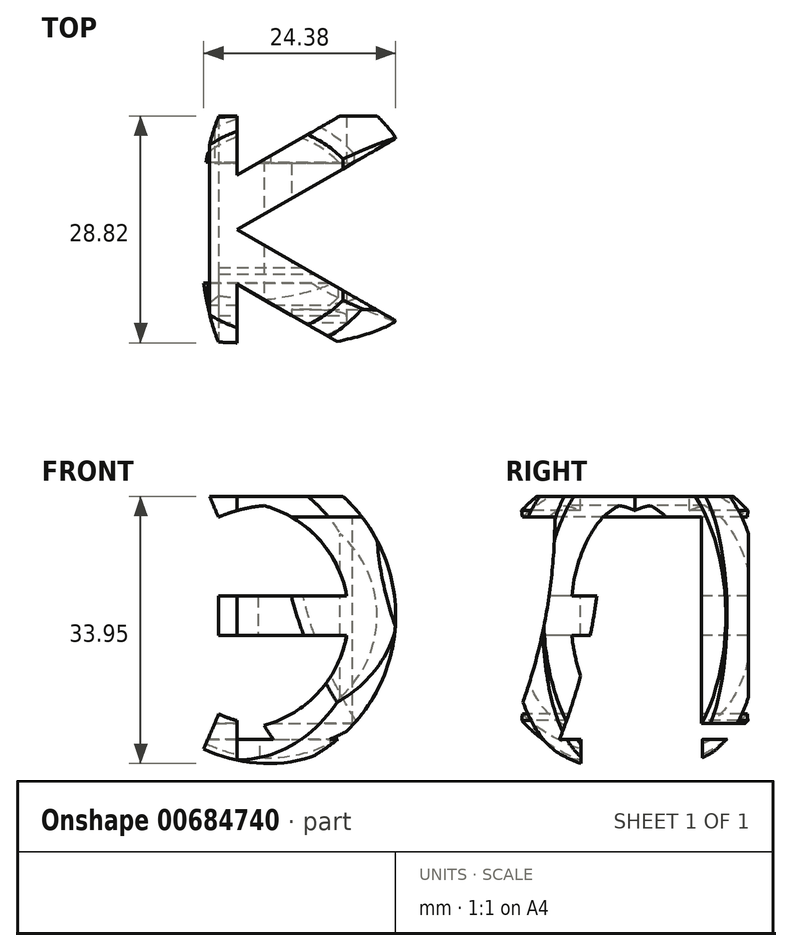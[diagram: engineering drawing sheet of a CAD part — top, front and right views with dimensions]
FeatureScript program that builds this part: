
annotation { "Feature Type Name" : "Feature", "Feature Type Description" : "" }
export const myFeature = defineFeature(function(context is Context, id is Id, definition is map)
    precondition{}
    {
        {
            var Q0;
            Q0=qCreatedBy(makeId("Front.planeOp"),FACE);
            var sketch = newSketch(context, id + "F0", { "sketchPlane" : qUnion([Q0])});
            skArc(sketch, "E0", {"start": v(20, 22.63) * mm, "mid": v(0, 42.63) * mm, "end": v(-20, 22.63) * mm});
            skLineSegment(sketch, "E1", {"start": v(20, 22.63) * mm, "end": v(0, 22.63) * mm});
            skLineSegment(sketch, "E2.MirrorCS", {"start": v(-20, 22.63) * mm, "end": v(0, 22.63) * mm});
            skSolve(sketch);
        }
        {
            var Q0;
            Q0=makeQuery(id+"F0.imprint","IMPRINT",FACE,{"disambiguationData":[TD([[makeQuery(id+"F0.imprint","IMPRINT",EDGE,{"derivedFrom":sQuery(id+"F0.wireOp",EDGE,"E0")}),1.0]])]});
            var Q1;
            Q1=sQuery(id+"F0.wireOp",EDGE,"E2.MirrorCS");
            revolve(context, id + "F1", {"entities" : qUnion([Q0]), "axis" : qUnion([Q1]), "revolveType" : RevolveType.FULL});
        }
        {
            var Q0;
            Q0=qCreatedBy(makeId("Top.planeOp"),FACE);
            cPlane(context, id + "F2", {"entities" : qUnion([Q0]), "cplaneType" : CPlaneType.OFFSET, "offset" : 43.3 * mm, "width" : 150 * mm, "height" : 150 * mm});
        }
        {
            var Q0;
            Q0=qCreatedBy(makeId("Right.planeOp"),FACE);
            cPlane(context, id + "F3", {"entities" : qUnion([Q0]), "cplaneType" : CPlaneType.OFFSET, "offset" : 22 * mm, "width" : 150 * mm, "height" : 150 * mm});
        }
        {
            var Q0;
            Q0=qCreatedBy(makeId("Front.planeOp"),FACE);
            cPlane(context, id + "F4", {"entities" : qUnion([Q0]), "cplaneType" : CPlaneType.OFFSET, "offset" : 22 * mm, "width" : 150 * mm, "height" : 150 * mm});
        }
        {
            var Q0;
            Q0=qCreatedBy(id+"F2.planeOp",FACE);
            var sketch = newSketch(context, id + "F5", { "sketchPlane" : qUnion([Q0])});
            skLineSegment(sketch, "E3", {"start": v(-11.94, 16.04) * mm, "end": v(-11.94, -16.04) * mm});
            skLineSegment(sketch, "E4", {"start": v(-11.94, -16.04) * mm, "end": v(-3.94, -16.04) * mm});
            skLineSegment(sketch, "E5", {"start": v(-3.94, -16.04) * mm, "end": v(-3.94, -6.92) * mm});
            skLineSegment(sketch, "E6", {"start": v(-3.94, -6.92) * mm, "end": v(11.94, -16.04) * mm});
            skLineSegment(sketch, "E7", {"start": v(16.28, -11.61) * mm, "end": v(-3.94, 0) * mm});
            skLineSegment(sketch, "E8", {"start": v(-3.94, 0) * mm, "end": v(16.28, 11.61) * mm});
            skLineSegment(sketch, "E9", {"start": v(11.94, 16.04) * mm, "end": v(-3.94, 6.92) * mm});
            skLineSegment(sketch, "E10", {"start": v(-3.94, 6.92) * mm, "end": v(-3.94, 16.04) * mm});
            skLineSegment(sketch, "E11", {"start": v(-3.94, 16.04) * mm, "end": v(-11.94, 16.04) * mm});
            skPoint(sketch, "E12.0", {"position": v(0, 0) * mm});
            skCircle(sketch, "E13", {"center": v(0, 0) * mm, "radius": 20 * mm});
            skPoint(sketch, "E14", {"position": v(-11.94, 0) * mm});
            skLineSegment(sketch, "E15", {"start": v(-11.94, 16.04) * mm, "end": v(17.44, 16.04) * mm, "construction": true});
            skLineSegment(sketch, "E16", {"start": v(-11.94, -16.04) * mm, "end": v(18.16, -16.04) * mm, "construction": true});
            skLineSegment(sketch, "E17", {"start": v(15.03, 16.04) * mm, "end": v(11.94, 16.04) * mm});
            skLineSegment(sketch, "E18", {"start": v(15.03, -16.04) * mm, "end": v(11.94, -16.04) * mm});
            skSolve(sketch);
        }
        {
            var Q0;
            {var subQ0=sQuery(id+"F5.wireOp",EDGE,"E3");Q0=makeQuery(id+"F5.imprint","IMPRINT",FACE,{"disambiguationData":[TD([[makeQuery(id+"F5.imprint","IMPRINT",EDGE,{"derivedFrom":subQ0}),-1.0]])]});}
            var Q1;
            {var subQ0=sQuery(id+"F5.wireOp",EDGE,"E4");Q1=makeQuery(id+"F5.imprint","IMPRINT",FACE,{"disambiguationData":[TD([[makeQuery(id+"F5.imprint","IMPRINT",EDGE,{"derivedFrom":subQ0}),-1.0]])]});}
            var Q2;
            {var subQ0=sQuery(id+"F5.wireOp",EDGE,"E7");Q2=makeQuery(id+"F5.imprint","IMPRINT",FACE,{"disambiguationData":[TD([[makeQuery(id+"F5.imprint","IMPRINT",EDGE,{"derivedFrom":subQ0}),-1.0]])]});}
            var Q3;
            {var subQ0=sQuery(id+"F5.wireOp",EDGE,"E9");Q3=makeQuery(id+"F5.imprint","IMPRINT",FACE,{"disambiguationData":[TD([[makeQuery(id+"F5.imprint","IMPRINT",EDGE,{"derivedFrom":subQ0}),-1.0]])]});}
            extrude(context, id + "F6", {"entities" : qUnion([Q0, Q1, Q2, Q3]), "operationType" : NewBodyOperationType.REMOVE, "oppositeDirection" : true, "depth" : 48.9 * mm, "offsetDistance" : 25 * mm});
        }
        {
            var Q0;
            Q0=qCreatedBy(id+"F4.planeOp",FACE);
            var sketch = newSketch(context, id + "F7", { "sketchPlane" : qUnion([Q0])});
            skPoint(sketch, "E19.0", {"position": v(0, 22.63) * mm});
            skCircle(sketch, "E20", {"center": v(0, 22.63) * mm, "radius": 20 * mm});
            skArc(sketch, "E21", {"start": v(0, 2.63) * mm, "mid": v(16.21, 22.63) * mm, "end": v(0, 42.63) * mm});
            skArc(sketch, "E22", {"start": v(0, 42.63) * mm, "mid": v(-4.41, 42.04) * mm, "end": v(-8.65, 40.67) * mm});
            skArc(sketch, "E23", {"start": v(-8.65, 4.6) * mm, "mid": v(-4.41, 3.22) * mm, "end": v(0, 2.63) * mm});
            skLineSegment(sketch, "E24", {"start": v(-8.65, 40.67) * mm, "end": v(-8.65, 4.6) * mm, "construction": true});
            skLineSegment(sketch, "E25", {"start": v(-6.65, 41.42) * mm, "end": v(-6.65, 3.77) * mm, "construction": true});
            skArc(sketch, "E26.0", {"start": v(-1.24, 8.5) * mm, "mid": v(10.21, 22.63) * mm, "end": v(-1.24, 36.76) * mm});
            skArc(sketch, "E27.0", {"start": v(0.28, 36.64) * mm, "mid": v(-3.08, 36.18) * mm, "end": v(-6.3, 35.14) * mm});
            skArc(sketch, "E28.0", {"start": v(-6.26, 10.1) * mm, "mid": v(-3.08, 9.07) * mm, "end": v(0.23, 8.63) * mm});
            skLineSegment(sketch, "E29", {"start": v(-8.65, 40.67) * mm, "end": v(-6.3, 35.14) * mm});
            skLineSegment(sketch, "E30", {"start": v(-8.65, 4.6) * mm, "end": v(-6.26, 10.1) * mm});
            skLineSegment(sketch, "E31", {"start": v(-6.26, 22.63) * mm, "end": v(10.21, 22.63) * mm, "construction": true});
            skLineSegment(sketch, "E32", {"start": v(-6.26, 25.13) * mm, "end": v(10, 25.13) * mm});
            skLineSegment(sketch, "E33", {"start": v(-6.26, 20.13) * mm, "end": v(10, 20.13) * mm});
            skLineSegment(sketch, "E34", {"start": v(-6.26, 25.13) * mm, "end": v(-6.26, 20.13) * mm});
            skSolve(sketch);
        }
        {
            var Q0;
            {var subQ0=sQuery(id+"F7.wireOp",EDGE,"E22");Q0=makeQuery(id+"F7.imprint","IMPRINT",FACE,{"disambiguationData":[TD([[makeQuery(id+"F7.imprint","IMPRINT",EDGE,{"derivedFrom":subQ0}),-1.0]])]});}
            var Q1;
            {var subQ0=sQuery(id+"F7.wireOp",EDGE,"E23");Q1=makeQuery(id+"F7.imprint","IMPRINT",FACE,{"disambiguationData":[TD([[makeQuery(id+"F7.imprint","IMPRINT",EDGE,{"derivedFrom":subQ0}),-1.0]])]});}
            var Q2;
            {var subQ0=sQuery(id+"F7.wireOp",EDGE,"E21");Q2=makeQuery(id+"F7.imprint","IMPRINT",FACE,{"disambiguationData":[TD([[makeQuery(id+"F7.imprint","IMPRINT",EDGE,{"derivedFrom":subQ0}),-1.0]])]});}
            var Q3;
            {var subQ0=sQuery(id+"F7.wireOp",EDGE,"E29");Q3=makeQuery(id+"F7.imprint","IMPRINT",FACE,{"disambiguationData":[TD([[makeQuery(id+"F7.imprint","IMPRINT",EDGE,{"derivedFrom":subQ0}),-1.0]])]});}
            extrude(context, id + "F8", {"entities" : qUnion([Q0, Q1, Q2, Q3]), "operationType" : NewBodyOperationType.REMOVE, "oppositeDirection" : true, "depth" : 73.9 * mm, "offsetDistance" : 25 * mm});
        }
        {
            var Q0;
            Q0=qCreatedBy(id+"F3.planeOp",FACE);
            var sketch = newSketch(context, id + "F9", { "sketchPlane" : qUnion([Q0])});
            skPoint(sketch, "E35.0", {"position": v(0, 22.63) * mm});
            skCircle(sketch, "E36", {"center": v(0, 22.63) * mm, "radius": 20 * mm});
            skLineSegment(sketch, "E37", {"start": v(-14.51, 36.4) * mm, "end": v(-14.51, 35.14) * mm});
            skLineSegment(sketch, "E38", {"start": v(-14.51, 35.14) * mm, "end": v(14.51, 35.14) * mm});
            skLineSegment(sketch, "E39", {"start": v(14.51, 35.14) * mm, "end": v(14.51, 36.4) * mm});
            skLineSegment(sketch, "E40", {"start": v(14.44, 35.14) * mm, "end": v(14.44, 8.93) * mm});
            skLineSegment(sketch, "E41", {"start": v(14.44, 8.93) * mm, "end": v(8.44, 8.93) * mm});
            skLineSegment(sketch, "E42", {"start": v(8.44, 8.93) * mm, "end": v(8.44, 35.14) * mm});
            skLineSegment(sketch, "E43", {"start": v(14.44, 8.93) * mm, "end": v(14.44, 6.93) * mm});
            skLineSegment(sketch, "E44", {"start": v(14.44, 6.93) * mm, "end": v(-15.78, 6.93) * mm});
            skLineSegment(sketch, "E45", {"start": v(-15.78, 6.93) * mm, "end": v(-15.78, 8.93) * mm});
            skLineSegment(sketch, "E46", {"start": v(-15.78, 8.93) * mm, "end": v(8.44, 8.93) * mm});
            skArc(sketch, "E47", {"start": v(-15.22, 8.93) * mm, "mid": v(-11.45, 21.8) * mm, "end": v(-10.15, 35.14) * mm});
            skArc(sketch, "E48.0", {"start": v(-9.56, 6.93) * mm, "mid": v(-5.3, 22.08) * mm, "end": v(-4.2, 37.78) * mm});
            skLineSegment(sketch, "E49", {"start": v(-14.51, 36.4) * mm, "end": v(-14.51, 37.78) * mm});
            skLineSegment(sketch, "E50", {"start": v(-14.51, 37.78) * mm, "end": v(14.51, 37.78) * mm});
            skLineSegment(sketch, "E51", {"start": v(14.51, 37.78) * mm, "end": v(14.51, 36.4) * mm});
            skLineSegment(sketch, "E52", {"start": v(-8.81, 6.93) * mm, "end": v(-8.81, 3.08) * mm});
            skLineSegment(sketch, "E53", {"start": v(-8.81, 3.08) * mm, "end": v(-6.81, 3.08) * mm});
            skLineSegment(sketch, "E54", {"start": v(-6.81, 3.08) * mm, "end": v(-6.81, 6.93) * mm});
            skLineSegment(sketch, "E55", {"start": v(8.58, 6.93) * mm, "end": v(8.58, 1.47) * mm});
            skLineSegment(sketch, "E56", {"start": v(8.58, 1.47) * mm, "end": v(10.58, 1.47) * mm});
            skLineSegment(sketch, "E57", {"start": v(10.58, 1.47) * mm, "end": v(10.58, 6.93) * mm});
            skSolve(sketch);
        }
        {
            var Q0;
            {var subQ0=sQuery(id+"F9.wireOp",EDGE,"E49");Q0=makeQuery(id+"F9.imprint","IMPRINT",FACE,{"disambiguationData":[TD([[makeQuery(id+"F9.imprint","IMPRINT",EDGE,{"derivedFrom":subQ0}),-1.0]])]});}
            var Q1;
            {var subQ0=sQuery(id+"F9.wireOp",EDGE,"E45");var subQ1=sQuery(id+"F9.wireOp",EDGE,"E36");var subQ2=makeQuery(id+"F9.imprint","INTERSECT",VERTEX,{"derivedFrom":[subQ1,subQ0]});Q1=makeQuery(id+"F9.imprint","IMPRINT",FACE,{"disambiguationData":[TD([[makeQuery(id+"F9.imprint","IMPRINT",EDGE,{"disambiguationData":[TD([[subQ2,-1.0]])],"derivedFrom":subQ1}),-1.0]])]});}
            var Q2;
            {var subQ5=sQuery(id+"F9.wireOp",EDGE,"E53");Q2=makeQuery(id+"F9.imprint","IMPRINT",FACE,{"disambiguationData":[TD([[makeQuery(id+"F9.imprint","IMPRINT",EDGE,{"derivedFrom":subQ5}),1.0]])]});}
            var Q3;
            {var subQ5=sQuery(id+"F9.wireOp",EDGE,"E56");Q3=makeQuery(id+"F9.imprint","IMPRINT",FACE,{"disambiguationData":[TD([[makeQuery(id+"F9.imprint","IMPRINT",EDGE,{"derivedFrom":subQ5}),1.0]])]});}
            var Q4;
            {var subQ6=sQuery(id+"F9.wireOp",EDGE,"E37");Q4=makeQuery(id+"F9.imprint","IMPRINT",FACE,{"disambiguationData":[TD([[makeQuery(id+"F9.imprint","IMPRINT",EDGE,{"derivedFrom":subQ6}),-1.0]])]});}
            var Q5;
            {var subQ0=sQuery(id+"F9.wireOp",EDGE,"E50");var subQ1=sQuery(id+"F9.wireOp",EDGE,"E36");var subQ2=makeQuery(id+"F9.imprint","INTERSECT",VERTEX,{"disambiguationData":[OD(0.0)],"derivedFrom":[subQ1,subQ0]});Q5=makeQuery(id+"F9.imprint","IMPRINT",FACE,{"disambiguationData":[TD([[makeQuery(id+"F9.imprint","IMPRINT",EDGE,{"disambiguationData":[TD([[subQ2,-1.0]])],"derivedFrom":subQ1}),1.0]])]});}
            var Q6;
            {var subQ1=sQuery(id+"F9.wireOp",EDGE,"E39");Q6=makeQuery(id+"F9.imprint","IMPRINT",FACE,{"disambiguationData":[TD([[makeQuery(id+"F9.imprint","IMPRINT",EDGE,{"derivedFrom":subQ1}),-1.0]])]});}
            var Q7;
            {var subQ0=sQuery(id+"F9.wireOp",EDGE,"E42");Q7=makeQuery(id+"F9.imprint","IMPRINT",FACE,{"disambiguationData":[TD([[makeQuery(id+"F9.imprint","IMPRINT",EDGE,{"derivedFrom":subQ0}),1.0]])]});}
            var Q8;
            {var subQ0=sQuery(id+"F9.wireOp",EDGE,"E54");var subQ1=sQuery(id+"F9.wireOp",EDGE,"E36");var subQ2=makeQuery(id+"F9.imprint","INTERSECT",VERTEX,{"derivedFrom":[subQ1,subQ0]});Q8=makeQuery(id+"F9.imprint","IMPRINT",FACE,{"disambiguationData":[TD([[makeQuery(id+"F9.imprint","IMPRINT",EDGE,{"disambiguationData":[TD([[subQ2,-1.0]])],"derivedFrom":subQ1}),1.0]])]});}
            var Q9;
            {var subQ0=sQuery(id+"F9.wireOp",EDGE,"E44");var subQ1=sQuery(id+"F9.wireOp",EDGE,"E36");var subQ2=makeQuery(id+"F9.imprint","INTERSECT",VERTEX,{"disambiguationData":[OD(0.0)],"derivedFrom":[subQ1,subQ0]});Q9=makeQuery(id+"F9.imprint","IMPRINT",FACE,{"disambiguationData":[TD([[makeQuery(id+"F9.imprint","IMPRINT",EDGE,{"disambiguationData":[TD([[subQ2,-1.0]])],"derivedFrom":subQ1}),1.0]])]});}
            extrude(context, id + "F10", {"entities" : qUnion([Q0, Q1, Q2, Q3, Q4, Q5, Q6, Q7, Q8, Q9]), "operationType" : NewBodyOperationType.REMOVE, "oppositeDirection" : true, "depth" : 48.9 * mm, "offsetDistance" : 25 * mm});
        }
    });
